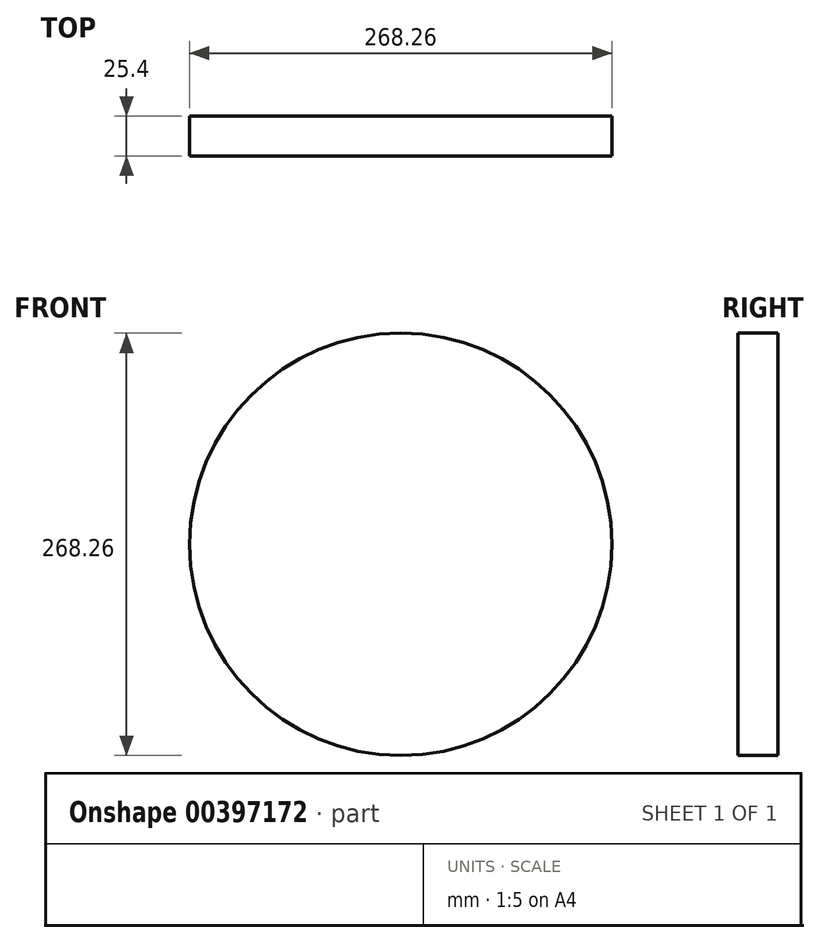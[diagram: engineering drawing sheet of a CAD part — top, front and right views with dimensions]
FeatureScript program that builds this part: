
annotation { "Feature Type Name" : "Feature", "Feature Type Description" : "" }
export const myFeature = defineFeature(function(context is Context, id is Id, definition is map)
    precondition{}
    {
        {
            var Q0;
            Q0=qCreatedBy(makeId("Front.planeOp"),FACE);
            var sketch = newSketch(context, id + "F0", { "sketchPlane" : qUnion([Q0])});
            skCircle(sketch, "E0", {"center": v(0, 0) * mm, "radius": 134.13 * mm});
            skSolve(sketch);
        }
        {
            var Q0;
            Q0=makeQuery(id+"F0.imprint","IMPRINT",FACE,{"disambiguationData":[TD([[makeQuery(id+"F0.imprint","IMPRINT",EDGE,{"derivedFrom":sQuery(id+"F0.wireOp",EDGE,"E0")}),1.0]])]});
            extrude(context, id + "F1", {"entities" : qUnion([Q0]), "depth" : 25.4 * mm});
        }
        {
            var Q0;
            Q0=makeQuery(id+"F1.opExtrude","CAP_FACE",FACE,{"disambiguationData":[OSD([sQuery(id+"F0.wireOp",EDGE,"E0")])],"isStart":false});
            var sketch = newSketch(context, id + "F2", { "sketchPlane" : qUnion([Q0])});
            skFitSpline(sketch, "E1", {"points": [v(-49.73, 86.1) * mm, v(-70.75, 83.1) * mm, v(-80.43, 68.42) * mm, v(-74.1, 56.74) * mm, v(-53.73, 51.06) * mm, v(-36.04, 52.73) * mm, v(-26.7, 66.41) * mm, v(-49.73, 86.1) * mm]});
            skFitSpline(sketch, "E2", {"points": [v(58.07, 86.1) * mm, v(78.43, 81.1) * mm, v(83.77, 73.76) * mm, v(86.44, 58.07) * mm, v(72.76, 53.4) * mm, v(62.08, 51.73) * mm, v(49.4, 52.4) * mm, v(38.05, 56.74) * mm, v(38.38, 62.74) * mm, v(40.38, 67.42) * mm, v(44.05, 71.75) * mm, v(58.07, 86.1) * mm]});
            skFitSpline(sketch, "E3", {"points": [v(0, 86.1) * mm, v(-4.67, 69.42) * mm, v(-16.35, 62.74) * mm, v(-19.36, 47.72) * mm, v(-5, 44.39) * mm, v(0, 47.72) * mm, v(2.34, 59.74) * mm, v(10.01, 55.73) * mm, v(7, 52.4) * mm, v(4.67, 42.72) * mm, v(14.35, 41.72) * mm, v(22.36, 47.4) * mm, v(24.36, 52.4) * mm, v(22.03, 57.74) * mm, v(16.69, 60.74) * mm, v(8.34, 63.08) * mm, v(0, 65.08) * mm, v(6, 72.42) * mm, v(18.02, 76.1) * mm, v(24.36, 76.1) * mm, v(32.37, 83.1) * mm, v(0, 86.1) * mm]});
            skFitSpline(sketch, "E4", {"points": [v(-92.45, 25.03) * mm, v(-85.1, 9.34) * mm, v(-86.1, 3.67) * mm, v(-93.78, -14.35) * mm, v(-98.12, -29.04) * mm, v(-98.79, -40.38) * mm, v(-97.79, -46.72) * mm, v(-94.45, -54.73) * mm, v(-86.1, -64.41) * mm, v(-59.74, -75.42) * mm, v(-55.07, -79.43) * mm, v(-37.71, -82.77) * mm, v(-30.7, -83.1) * mm, v(-17.02, -76.1) * mm, v(3, -76.76) * mm, v(37.38, -83.77) * mm, v(42.72, -86.77) * mm, v(78.76, -51.4) * mm, v(106.13, -41.05) * mm, v(118.48, -32.37) * mm, v(118.81, -8.34) * mm, v(115.14, 0) * mm, v(113.47, 3.34) * mm, v(109.47, 15.69) * mm, v(103.46, 31.7) * mm, v(108.13, 39.05) * mm, v(106.13, 44.05) * mm, v(90.1, 41.05) * mm, v(89.78, 36.04) * mm, v(91.78, 21.03) * mm, v(88.77, 16.02) * mm, v(83.1, 12.68) * mm, v(70.42, 15.02) * mm, v(65.08, 16.69) * mm, v(52.06, 21.7) * mm, v(45.39, 23.7) * mm, v(31.37, 19.36) * mm, v(20.36, 13.35) * mm, v(13.02, 5.34) * mm, v(-17.69, -10.68) * mm, v(-20.36, -12.35) * mm, v(-29.37, -11.35) * mm, v(-35.38, -9.34) * mm, v(-46.72, -5) * mm, v(-55.07, 0) * mm, v(-59.74, 8.34) * mm, v(-59.74, 14.35) * mm, v(-60.07, 23.03) * mm, v(-60.74, 27.37) * mm, v(-68.75, 32.7) * mm, v(-81.43, 34.38) * mm, v(-87.1, 35.71) * mm, v(-89.78, 37.05) * mm, v(-96.12, 49.06) * mm, v(-101.8, 46.72) * mm, v(-96.78, 28.37) * mm, v(-92.45, 25.03) * mm]});
            skFitSpline(sketch, "E5", {"points": [v(-72.42, 93.78) * mm, v(-61.07, 95.12) * mm, v(-42.72, 94.11) * mm, v(-23.03, 86.1) * mm, v(-26.7, 86.1) * mm, v(-47.4, 91.11) * mm, v(-68.42, 89.44) * mm, v(-72.42, 93.78) * mm]});
            skFitSpline(sketch, "E6", {"points": [v(45.39, 92.78) * mm, v(73.76, 92.45) * mm, v(88.77, 86.1) * mm, v(91.11, 79.43) * mm, v(80.1, 86.1) * mm, v(69.75, 88.77) * mm, v(58.07, 89.78) * mm, v(45.39, 92.78) * mm]});
            skFitSpline(sketch, "E7", {"points": [v(-55.07, 69.42) * mm, v(-61.4, 69.42) * mm, v(-62.08, 66.41) * mm, v(-49.73, 61.4) * mm, v(-49.73, 66.41) * mm, v(-55.07, 69.42) * mm]});
            skFitSpline(sketch, "E8", {"points": [v(65.41, 72.09) * mm, v(58.07, 69.42) * mm, v(49.4, 60.4) * mm, v(67.42, 59.4) * mm, v(79.76, 66.41) * mm, v(74.1, 75.42) * mm, v(65.41, 80.76) * mm, v(58.07, 79.43) * mm, v(60.74, 75.1) * mm, v(65.41, 72.09) * mm]});
            skFitSpline(sketch, "E9", {"points": [v(-77.1, -51.73) * mm, v(-78.1, -51.73) * mm, v(-55.07, -46.39) * mm, v(-26.7, -51.73) * mm, v(-32.7, -59.74) * mm, v(-33.37, -60.4) * mm, v(-23.7, -61.4) * mm, v(-13.35, -62.08) * mm, v(-11.68, -51.06) * mm, v(0, -54.4) * mm, v(0, -65.08) * mm, v(14.68, -64.75) * mm, v(15.69, -59.74) * mm, v(15.02, -53.06) * mm, v(25.7, -53.06) * mm, v(28.03, -58.07) * mm, v(29.7, -63.74) * mm, v(36.38, -64.41) * mm, v(37.05, -64.08) * mm, v(39.38, -58.4) * mm, v(37.71, -54.07) * mm, v(37.71, -52.4) * mm, v(41.38, -50.4) * mm, v(49.4, -49.73) * mm, v(49.4, -52.73) * mm, v(53.4, -57.4) * mm, v(64.08, -54.4) * mm, v(64.08, -53.73) * mm, v(65.41, -48.06) * mm, v(65.41, -43.39) * mm, v(66.41, -38.38) * mm, v(66.41, -37.05) * mm, v(66.41, -27.37) * mm, v(66.41, -27.03) * mm, v(67.42, -18.02) * mm, v(67.42, -11.35) * mm, v(67.42, -3) * mm, v(67.42, -2.67) * mm, v(66.75, 0) * mm, v(62.74, 4.34) * mm, v(58.07, 7) * mm, v(49.4, 0) * mm, v(52.06, -6) * mm, v(49.4, -11.35) * mm, v(42.72, -11.35) * mm, v(41.38, -11.35) * mm, v(32.7, -5.67) * mm, v(30.37, 0) * mm, v(30.37, 3) * mm, v(23.03, 0) * mm, v(20.7, -4.67) * mm, v(19.7, -8) * mm, v(19.7, -11.35) * mm, v(18.36, -11.35) * mm, v(9.68, -15.35) * mm, v(9.01, -15.35) * mm, v(3, -15.35) * mm, v(3, -14.68) * mm, v(3, -11.35) * mm, v(-4.67, -14.02) * mm, v(-4.67, -16.02) * mm, v(-4.67, -18.36) * mm, v(-4.67, -20.7) * mm, v(-13.35, -22.7) * mm, v(-17.35, -22.7) * mm, v(-19.02, -22.03) * mm, v(-19.02, -21.36) * mm], "startDerivative": vector(-222.74, -20.95) * mm, "endDerivative": vector(36.05, 130.63) * mm});
            skLineSegment(sketch, "E10.bottom", {"start": v(52.25, -61.35) * mm, "end": v(-366.41, -61.35) * mm});
            skLineSegment(sketch, "E10.top", {"start": v(52.25, 370.33) * mm, "end": v(-366.41, 370.33) * mm});
            skLineSegment(sketch, "E10.left", {"start": v(52.25, -61.35) * mm, "end": v(52.25, 370.33) * mm});
            skLineSegment(sketch, "E10.right", {"start": v(-366.41, -61.35) * mm, "end": v(-366.41, 370.33) * mm});
            skPoint(sketch, "E10.middle", {"position": v(-157.08, 154.49) * mm});
            skSolve(sketch);
        }
        {
            var Q0;
            Q0=sQuery(id+"F2.wireOp",EDGE,"E4");
            var Q1;
            Q1=sQuery(id+"F2.wireOp",EDGE,"E1");
            var Q2;
            Q2=sQuery(id+"F2.wireOp",EDGE,"E3");
            var Q3;
            Q3=sQuery(id+"F2.wireOp",EDGE,"E5");
            var Q4;
            Q4=sQuery(id+"F2.wireOp",EDGE,"E7");
            extrude(context, id + "F3", {"bodyType" : ToolBodyType.SURFACE, "surfaceEntities" : qUnion([Q0, Q1, Q2, Q3, Q4]), "depth" : 25.4 * mm});
        }
    });
